# Revit family: Genie_Site_ScissorLift_GS1330a
name_source: partatom
category: Site
revit_build: Autodesk Revit 2018 (Build: 20190510_1515(x64)
units: mm (PartAtom-declared; Revit-internal decimal feet)

## family parameters
Always vertical = Yes
Cut with Voids When Loaded = No
OmniClass Number = 23.50.85.17.11
OmniClass Title = Electric and Battery Telescoping Platforms
Part Type = Normal
Round Connector Dimension = Use Diameter
Shared = No
Work Plane-Based = No

## types (1)
- GS-1330
    Assembly Code = E1030900
    AssetType = Fixed
    BIMObjectName = Genie_Site_ScissorLift_GS1330
    ClassificationName = Uniclass2015
    ClassificationValue = Pr_65_80_47_95
    Color = Grey & Blue
    Cost = 0 $
    Description = The Genie® GS™-1330m scissor lift offers a maximum platform height of 12.8 ft (3.9 m) and a maximum working height of 18.8 ft (5.9 m), with a 2-person, 500-lb (227 kg) capacity and weighing in at only 1,950 lb (885 kg). The Genie GS-1330m scissor lift is equipped with an efficient, all-electric DC drive system that offers productive power for getting around indoor jobsites with quiet, zero-emissions operation.
    DocumentationLiterature = https://www.genielift.com
    DocumentationTechnical = https://www.genielift.com
    DurationUnit = Years
    ExpectedLife = 0
    Features = Compact dimensions ideal for low level and tight access applications. Efficient electric drive system provides maximum runtime per charge. 2 person platform occupancy 500 lb (227 kg) max lift capacity. Lift weight only 1,950 lb (885 kg). Smooth and responsive proportional lift and drive controls. Commonality in design and parts with other Genie scissor lifts. Utilized Genie Smartlink™.
    Finish = Painted Steel
    IfcExportAs = IfcTransportElement
    IfcExportType = IfcTransportElementType
    Keynote = X
    Manufacturer = Genie
    ManufacturerName = Genie
    Material = Painted Steel
    Model = Genie - Scissor Lift
    ModelNumber = GS-1330
    ModelReference = Genie - Scissor Lift
    NBSDescription = Vertical lifting platforms
    NBSObjectName = Genie - Vertical lifting platforms
    NBSReference = 90-80-65/350
    NominalDepth = 780 mm  [stored 2.55906 ft]
    NominalHeight = 2020 mm  [stored 6.6273 ft]
    NominalLength = 1410 mm  [stored 4.62598 ft]
    PrimaryMaterial = Steel, Paint Finish, Blue, Genie
    ProductionYear = 2019
    ReplacementCost = 0
    SecondaryMaterial = Steel, Paint Finish, Grey, Genie
    Size = 780mm x 2020mm x 1410mm
    Type Comments = GS-1330
    TypeName = Genie - Scissor Lift
    URL = http://www.genielift.co.uk
    WarrantyDurationLabor = 0
    WarrantyDurationParts = 0
    WarrantyDurationUnit = Years
    WarrantyGuarantorLabor = http://www.genielift.co.uk
    WarrantyGuarantorParts = http://www.genielift.co.uk
    _BSBibleVersion = 15
    _BimSpecGuid = 0
    _CurrentRevision = 1
    _DistributedBy = www.bimstore.co.uk

note: [stored X ft] marks values corroborated as IEEE doubles in the binary element streams (Revit-internal decimal feet)

## geometry (parser evidence)
native form markers: Sweep x19
no freeform markers — native parametric forms only
